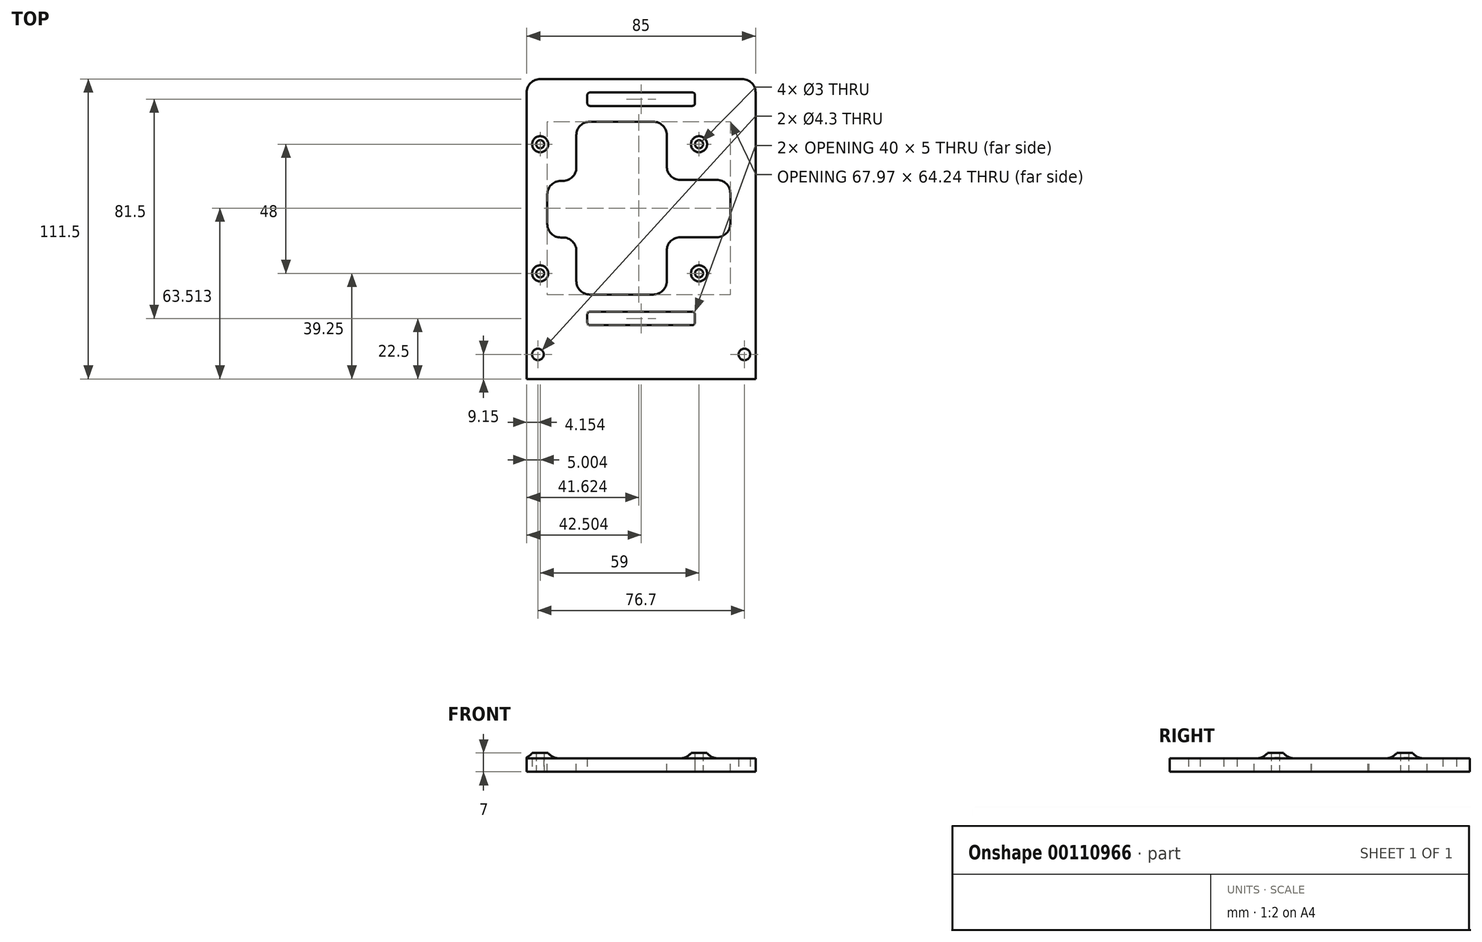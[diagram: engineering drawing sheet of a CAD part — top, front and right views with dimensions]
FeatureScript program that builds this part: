
annotation { "Feature Type Name" : "Feature", "Feature Type Description" : "" }
export const myFeature = defineFeature(function(context is Context, id is Id, definition is map)
    precondition{}
    {
        {
            var Q0;
            Q0=qCreatedBy(makeId("Top.planeOp"),FACE);
            var sketch = newSketch(context, id + "F0", { "sketchPlane" : qUnion([Q0])});
            skLineSegment(sketch, "E0.bottom", {"start": v(-29.26, 0) * mm, "end": v(55.74, 0) * mm});
            skLineSegment(sketch, "E0.top", {"start": v(-29.26, 111.5) * mm, "end": v(55.74, 111.5) * mm});
            skLineSegment(sketch, "E0.left", {"start": v(-29.26, 0) * mm, "end": v(-29.26, 111.5) * mm});
            skLineSegment(sketch, "E0.right", {"start": v(55.74, 0) * mm, "end": v(55.74, 111.5) * mm});
            skLineSegment(sketch, "E1.top", {"start": v(-29.26, 20) * mm, "end": v(55.74, 20) * mm});
            skLineSegment(sketch, "E1.left", {"start": v(-29.26, 0) * mm, "end": v(-29.26, 20) * mm});
            skLineSegment(sketch, "E1.right", {"start": v(55.74, 0) * mm, "end": v(55.74, 20) * mm});
            skLineSegment(sketch, "E2.bottom", {"start": v(-6.76, 20) * mm, "end": v(33.24, 20) * mm});
            skLineSegment(sketch, "E2.top", {"start": v(-6.76, 25) * mm, "end": v(33.24, 25) * mm});
            skLineSegment(sketch, "E2.left", {"start": v(-6.76, 20) * mm, "end": v(-6.76, 25) * mm});
            skLineSegment(sketch, "E2.right", {"start": v(33.24, 20) * mm, "end": v(33.24, 25) * mm});
            skPoint(sketch, "E3", {"position": v(13.24, 111.5) * mm});
            skPoint(sketch, "E4", {"position": v(13.24, 25) * mm});
            skLineSegment(sketch, "E5.top", {"start": v(-29.26, 106.5) * mm, "end": v(55.74, 106.5) * mm});
            skLineSegment(sketch, "E5.left", {"start": v(-29.26, 111.5) * mm, "end": v(-29.26, 106.5) * mm});
            skLineSegment(sketch, "E5.right", {"start": v(55.74, 111.5) * mm, "end": v(55.74, 106.5) * mm});
            skCircle(sketch, "E6", {"center": v(13.24, 63.25) * mm, "radius": 5 * mm});
            skCircle(sketch, "E7", {"center": v(23.24, 53.25) * mm, "radius": 1.5 * mm});
            skCircle(sketch, "E8", {"center": v(3.24, 53.25) * mm, "radius": 1.5 * mm});
            skCircle(sketch, "E9", {"center": v(3.24, 73.25) * mm, "radius": 1.5 * mm});
            skCircle(sketch, "E10", {"center": v(23.24, 73.25) * mm, "radius": 1.5 * mm});
            skLineSegment(sketch, "E11", {"start": v(23.24, 73.25) * mm, "end": v(23.24, 53.25) * mm, "construction": true});
            skLineSegment(sketch, "E12", {"start": v(3.24, 73.25) * mm, "end": v(23.24, 73.25) * mm, "construction": true});
            skPoint(sketch, "E13", {"position": v(23.24, 63.25) * mm});
            skPoint(sketch, "E14", {"position": v(13.24, 73.25) * mm});
            skLineSegment(sketch, "E15", {"start": v(23.24, 73.25) * mm, "end": v(23.24, 106.5) * mm, "construction": true});
            skLineSegment(sketch, "E16", {"start": v(23.24, 53.25) * mm, "end": v(23.24, 20) * mm, "construction": true});
            skCircle(sketch, "E17", {"center": v(-24.26, 87.25) * mm, "radius": 3 * mm});
            skCircle(sketch, "E18", {"center": v(-24.26, 39.25) * mm, "radius": 3 * mm});
            skCircle(sketch, "E19", {"center": v(34.74, 87.25) * mm, "radius": 3 * mm});
            skCircle(sketch, "E20", {"center": v(34.74, 39.25) * mm, "radius": 3 * mm});
            skLineSegment(sketch, "E21", {"start": v(-24.26, 87.25) * mm, "end": v(34.74, 87.25) * mm, "construction": true});
            skLineSegment(sketch, "E22", {"start": v(34.74, 87.25) * mm, "end": v(34.74, 39.25) * mm, "construction": true});
            skCircle(sketch, "E23", {"center": v(-24.26, 87.25) * mm, "radius": 1.5 * mm});
            skCircle(sketch, "E24", {"center": v(-24.26, 39.25) * mm, "radius": 1.5 * mm});
            skCircle(sketch, "E25", {"center": v(34.74, 39.25) * mm, "radius": 1.5 * mm});
            skCircle(sketch, "E26", {"center": v(34.74, 87.25) * mm, "radius": 1.5 * mm});
            skLineSegment(sketch, "E27", {"start": v(34.74, 39.25) * mm, "end": v(34.74, 20) * mm, "construction": true});
            skLineSegment(sketch, "E28", {"start": v(34.74, 87.25) * mm, "end": v(34.74, 106.5) * mm, "construction": true});
            skCircle(sketch, "E29", {"center": v(-25.1, 9.15) * mm, "radius": 2.15 * mm});
            skCircle(sketch, "E30", {"center": v(51.6, 9.15) * mm, "radius": 2.15 * mm});
            skLineSegment(sketch, "E31.bottom", {"start": v(-6.76, 106.5) * mm, "end": v(33.24, 106.5) * mm});
            skLineSegment(sketch, "E31.top", {"start": v(-6.76, 101.5) * mm, "end": v(33.24, 101.5) * mm});
            skLineSegment(sketch, "E31.left", {"start": v(-6.76, 106.5) * mm, "end": v(-6.76, 101.5) * mm});
            skLineSegment(sketch, "E31.right", {"start": v(33.24, 106.5) * mm, "end": v(33.24, 101.5) * mm});
            skSolve(sketch);
        }
        {
            var Q0;
            Q0=qSketchRegion(id+"F0",true);
            var Q1;
            Q1=makeQuery(id+"F0.imprint","IMPRINT",FACE,{"disambiguationData":[TD([[makeQuery(id+"F0.imprint","IMPRINT",EDGE,{"derivedFrom":sQuery(id+"F0.wireOp",EDGE,"E18")}),1.0]])]});
            var Q2;
            Q2=makeQuery(id+"F0.imprint","IMPRINT",FACE,{"disambiguationData":[TD([[makeQuery(id+"F0.imprint","IMPRINT",EDGE,{"derivedFrom":sQuery(id+"F0.wireOp",EDGE,"E17")}),1.0]])]});
            var Q3;
            Q3=makeQuery(id+"F0.imprint","IMPRINT",FACE,{"disambiguationData":[TD([[makeQuery(id+"F0.imprint","IMPRINT",EDGE,{"derivedFrom":sQuery(id+"F0.wireOp",EDGE,"E20")}),1.0]])]});
            var Q4;
            Q4=makeQuery(id+"F0.imprint","IMPRINT",FACE,{"disambiguationData":[TD([[makeQuery(id+"F0.imprint","IMPRINT",EDGE,{"derivedFrom":sQuery(id+"F0.wireOp",EDGE,"E19")}),1.0]])]});
            var Q5;
            Q5=makeQuery(id+"F0.imprint","IMPRINT",FACE,{"disambiguationData":[TD([[makeQuery(id+"F0.imprint","IMPRINT",EDGE,{"derivedFrom":sQuery(id+"F0.wireOp",EDGE,"E6")}),1.0]])]});
            var Q6;
            Q6=makeQuery(id+"F0.imprint","IMPRINT",FACE,{"disambiguationData":[TD([[makeQuery(id+"F0.imprint","IMPRINT",EDGE,{"derivedFrom":sQuery(id+"F0.wireOp",EDGE,"E9")}),1.0]])]});
            var Q7;
            Q7=makeQuery(id+"F0.imprint","IMPRINT",FACE,{"disambiguationData":[TD([[makeQuery(id+"F0.imprint","IMPRINT",EDGE,{"derivedFrom":sQuery(id+"F0.wireOp",EDGE,"E8")}),1.0]])]});
            var Q8;
            Q8=makeQuery(id+"F0.imprint","IMPRINT",FACE,{"disambiguationData":[TD([[makeQuery(id+"F0.imprint","IMPRINT",EDGE,{"derivedFrom":sQuery(id+"F0.wireOp",EDGE,"E7")}),1.0]])]});
            var Q9;
            Q9=makeQuery(id+"F0.imprint","IMPRINT",FACE,{"disambiguationData":[TD([[makeQuery(id+"F0.imprint","IMPRINT",EDGE,{"derivedFrom":sQuery(id+"F0.wireOp",EDGE,"E10")}),1.0]])]});
            extrude(context, id + "F1", {"entities" : qUnion([Q0, Q1, Q2, Q3, Q4, Q5, Q6, Q7, Q8, Q9]), "depth" : 5 * mm});
        }
        {
            var Q0;
            Q0=makeQuery(id+"F1.opExtrude","SWEPT_EDGE",EDGE,{"disambiguationData":[OSD([sQuery(id+"F0.wireOp",EDGE,"E2.top"),sQuery(id+"F0.wireOp",EDGE,"E2.left")])]});
            var Q1;
            Q1=makeQuery(id+"F1.opExtrude","SWEPT_EDGE",EDGE,{"disambiguationData":[OSD([sQuery(id+"F0.wireOp",EDGE,"E2.top"),sQuery(id+"F0.wireOp",EDGE,"E2.right")])]});
            var Q2;
            Q2=makeQuery(id+"F1.opExtrude","SWEPT_EDGE",EDGE,{"disambiguationData":[OSD([sQuery(id+"F0.wireOp",EDGE,"E1.top"),sQuery(id+"F0.wireOp",EDGE,"E2.bottom"),sQuery(id+"F0.wireOp",EDGE,"E2.left")])]});
            var Q3;
            Q3=makeQuery(id+"F1.opExtrude","SWEPT_EDGE",EDGE,{"disambiguationData":[OSD([sQuery(id+"F0.wireOp",EDGE,"E1.top"),sQuery(id+"F0.wireOp",EDGE,"E2.bottom"),sQuery(id+"F0.wireOp",EDGE,"E2.right")])]});
            var Q4;
            Q4=makeQuery(id+"F1.opExtrude","SWEPT_EDGE",EDGE,{"disambiguationData":[OSD([sQuery(id+"F0.wireOp",EDGE,"E31.top"),sQuery(id+"F0.wireOp",EDGE,"E31.left")])]});
            var Q5;
            Q5=makeQuery(id+"F1.opExtrude","SWEPT_EDGE",EDGE,{"disambiguationData":[OSD([sQuery(id+"F0.wireOp",EDGE,"E5.top"),sQuery(id+"F0.wireOp",EDGE,"E31.bottom"),sQuery(id+"F0.wireOp",EDGE,"E31.left")])]});
            var Q6;
            Q6=makeQuery(id+"F1.opExtrude","SWEPT_EDGE",EDGE,{"disambiguationData":[OSD([sQuery(id+"F0.wireOp",EDGE,"E5.top"),sQuery(id+"F0.wireOp",EDGE,"E31.bottom"),sQuery(id+"F0.wireOp",EDGE,"E31.right")])]});
            var Q7;
            Q7=makeQuery(id+"F1.opExtrude","SWEPT_EDGE",EDGE,{"disambiguationData":[OSD([sQuery(id+"F0.wireOp",EDGE,"E31.top"),sQuery(id+"F0.wireOp",EDGE,"E31.right")])]});
            fillet(context, id + "F2", {"entities" : qUnion([Q0, Q1, Q2, Q3, Q4, Q5, Q6, Q7]), "radius" : 1 * mm, "tangentPropagation" : true, "allowEdgeOverflow" : false});
        }
        {
            var Q0;
            {var subQ0=sQuery(id+"F0.wireOp",EDGE,"E5.left");var subQ1=sQuery(id+"F0.wireOp",EDGE,"E0.top");Q0=makeQuery(id+"FNY0aRx3992dt0J_1.boolean.opBoolean","MERGE",EDGE,{"derivedFrom":[makeQuery(id+"F1.opExtrude","SWEPT_EDGE",EDGE,{"disambiguationData":[OSD([subQ1,subQ0])]}),makeQuery(id+"FNY0aRx3992dt0J_1.opExtrude","SWEPT_EDGE",EDGE,{"disambiguationData":[OSD([subQ1,subQ0])]})]});}
            var Q1;
            {var subQ0=sQuery(id+"F0.wireOp",EDGE,"E1.left");var subQ1=sQuery(id+"F0.wireOp",EDGE,"E0.bottom");Q1=makeQuery(id+"FNY0aRx3992dt0J_1.boolean.opBoolean","MERGE",EDGE,{"derivedFrom":[makeQuery(id+"F1.opExtrude","SWEPT_EDGE",EDGE,{"disambiguationData":[OSD([subQ1,subQ0])]}),makeQuery(id+"FNY0aRx3992dt0J_1.opExtrude","SWEPT_EDGE",EDGE,{"disambiguationData":[OSD([subQ1,subQ0])]})]});}
            var Q2;
            Q2=makeQuery(id+"F1.opExtrude","SWEPT_EDGE",EDGE,{"disambiguationData":[OSD([sQuery(id+"F0.wireOp",EDGE,"E0.bottom"),sQuery(id+"F0.wireOp",EDGE,"E1.left")])]});
            var Q3;
            Q3=makeQuery(id+"F1.opExtrude","SWEPT_EDGE",EDGE,{"disambiguationData":[OSD([sQuery(id+"F0.wireOp",EDGE,"E0.bottom"),sQuery(id+"F0.wireOp",EDGE,"E1.right")])]});
            var Q4;
            Q4=makeQuery(id+"F1.opExtrude","SWEPT_EDGE",EDGE,{"disambiguationData":[OSD([sQuery(id+"F0.wireOp",EDGE,"E0.top"),sQuery(id+"F0.wireOp",EDGE,"E5.right")])]});
            fillet(context, id + "F3", {"entities" : qUnion([Q0, Q1, Q2, Q3, Q4]), "radius" : 5 * mm, "tangentPropagation" : true, "allowEdgeOverflow" : false});
        }
        {
            var Q0;
            Q0=makeQuery(id+"F0.imprint","IMPRINT",FACE,{"disambiguationData":[TD([[makeQuery(id+"F0.imprint","IMPRINT",EDGE,{"derivedFrom":sQuery(id+"F0.wireOp",EDGE,"E17")}),1.0]])]});
            var Q1;
            Q1=makeQuery(id+"F0.imprint","IMPRINT",FACE,{"disambiguationData":[TD([[makeQuery(id+"F0.imprint","IMPRINT",EDGE,{"derivedFrom":sQuery(id+"F0.wireOp",EDGE,"E18")}),1.0]])]});
            var Q2;
            Q2=makeQuery(id+"F0.imprint","IMPRINT",FACE,{"disambiguationData":[TD([[makeQuery(id+"F0.imprint","IMPRINT",EDGE,{"derivedFrom":sQuery(id+"F0.wireOp",EDGE,"E19")}),1.0]])]});
            var Q3;
            Q3=makeQuery(id+"F0.imprint","IMPRINT",FACE,{"disambiguationData":[TD([[makeQuery(id+"F0.imprint","IMPRINT",EDGE,{"derivedFrom":sQuery(id+"F0.wireOp",EDGE,"E20")}),1.0]])]});
            extrude(context, id + "F4", {"entities" : qUnion([Q0, Q1, Q2, Q3]), "operationType" : NewBodyOperationType.ADD, "depth" : 7 * mm});
        }
        {
            var Q0;
            Q0=makeQuery(id+"F4.boolean.opBoolean","INTERSECT",EDGE,{"derivedFrom":[makeQuery(id+"F1.opExtrude","CAP_FACE",FACE,{"disambiguationData":[OSD([sQuery(id+"F0.wireOp",EDGE,"E0.left"),sQuery(id+"F0.wireOp",EDGE,"E0.right"),sQuery(id+"F0.wireOp",EDGE,"E0.bottom"),sQuery(id+"F0.wireOp",EDGE,"E1.left"),sQuery(id+"F0.wireOp",EDGE,"E1.right"),sQuery(id+"F0.wireOp",EDGE,"E2.bottom"),sQuery(id+"F0.wireOp",EDGE,"E2.top"),sQuery(id+"F0.wireOp",EDGE,"E2.left"),sQuery(id+"F0.wireOp",EDGE,"E2.right"),sQuery(id+"F0.wireOp",EDGE,"E0.top"),sQuery(id+"F0.wireOp",EDGE,"E5.left"),sQuery(id+"F0.wireOp",EDGE,"E5.right"),sQuery(id+"F0.wireOp",EDGE,"E6"),sQuery(id+"F0.wireOp",EDGE,"E7"),sQuery(id+"F0.wireOp",EDGE,"E8"),sQuery(id+"F0.wireOp",EDGE,"E9"),sQuery(id+"F0.wireOp",EDGE,"E10")])],"isStart":false}),makeQuery(id+"F4.opExtrude","SWEPT_FACE",FACE,{"disambiguationData":[OSD([sQuery(id+"F0.wireOp",EDGE,"E17")])]})]});
            var Q1;
            Q1=makeQuery(id+"F4.boolean.opBoolean","INTERSECT",EDGE,{"derivedFrom":[makeQuery(id+"F1.opExtrude","CAP_FACE",FACE,{"disambiguationData":[OSD([sQuery(id+"F0.wireOp",EDGE,"E0.left"),sQuery(id+"F0.wireOp",EDGE,"E0.right"),sQuery(id+"F0.wireOp",EDGE,"E0.bottom"),sQuery(id+"F0.wireOp",EDGE,"E1.left"),sQuery(id+"F0.wireOp",EDGE,"E1.right"),sQuery(id+"F0.wireOp",EDGE,"E2.bottom"),sQuery(id+"F0.wireOp",EDGE,"E2.top"),sQuery(id+"F0.wireOp",EDGE,"E2.left"),sQuery(id+"F0.wireOp",EDGE,"E2.right"),sQuery(id+"F0.wireOp",EDGE,"E0.top"),sQuery(id+"F0.wireOp",EDGE,"E5.left"),sQuery(id+"F0.wireOp",EDGE,"E5.right"),sQuery(id+"F0.wireOp",EDGE,"E6"),sQuery(id+"F0.wireOp",EDGE,"E7"),sQuery(id+"F0.wireOp",EDGE,"E8"),sQuery(id+"F0.wireOp",EDGE,"E9"),sQuery(id+"F0.wireOp",EDGE,"E10")])],"isStart":false}),makeQuery(id+"F4.opExtrude","SWEPT_FACE",FACE,{"disambiguationData":[OSD([sQuery(id+"F0.wireOp",EDGE,"E18")])]})]});
            var Q2;
            Q2=makeQuery(id+"F4.boolean.opBoolean","INTERSECT",EDGE,{"derivedFrom":[makeQuery(id+"F1.opExtrude","CAP_FACE",FACE,{"disambiguationData":[OSD([sQuery(id+"F0.wireOp",EDGE,"E0.left"),sQuery(id+"F0.wireOp",EDGE,"E0.right"),sQuery(id+"F0.wireOp",EDGE,"E0.bottom"),sQuery(id+"F0.wireOp",EDGE,"E1.left"),sQuery(id+"F0.wireOp",EDGE,"E1.right"),sQuery(id+"F0.wireOp",EDGE,"E2.bottom"),sQuery(id+"F0.wireOp",EDGE,"E2.top"),sQuery(id+"F0.wireOp",EDGE,"E2.left"),sQuery(id+"F0.wireOp",EDGE,"E2.right"),sQuery(id+"F0.wireOp",EDGE,"E0.top"),sQuery(id+"F0.wireOp",EDGE,"E5.left"),sQuery(id+"F0.wireOp",EDGE,"E5.right"),sQuery(id+"F0.wireOp",EDGE,"E6"),sQuery(id+"F0.wireOp",EDGE,"E7"),sQuery(id+"F0.wireOp",EDGE,"E8"),sQuery(id+"F0.wireOp",EDGE,"E9"),sQuery(id+"F0.wireOp",EDGE,"E10")])],"isStart":false}),makeQuery(id+"F4.opExtrude","SWEPT_FACE",FACE,{"disambiguationData":[OSD([sQuery(id+"F0.wireOp",EDGE,"E20")])]})]});
            var Q3;
            Q3=makeQuery(id+"F4.boolean.opBoolean","INTERSECT",EDGE,{"derivedFrom":[makeQuery(id+"F1.opExtrude","CAP_FACE",FACE,{"disambiguationData":[OSD([sQuery(id+"F0.wireOp",EDGE,"E0.left"),sQuery(id+"F0.wireOp",EDGE,"E0.right"),sQuery(id+"F0.wireOp",EDGE,"E0.bottom"),sQuery(id+"F0.wireOp",EDGE,"E1.left"),sQuery(id+"F0.wireOp",EDGE,"E1.right"),sQuery(id+"F0.wireOp",EDGE,"E2.bottom"),sQuery(id+"F0.wireOp",EDGE,"E2.top"),sQuery(id+"F0.wireOp",EDGE,"E2.left"),sQuery(id+"F0.wireOp",EDGE,"E2.right"),sQuery(id+"F0.wireOp",EDGE,"E0.top"),sQuery(id+"F0.wireOp",EDGE,"E5.left"),sQuery(id+"F0.wireOp",EDGE,"E5.right"),sQuery(id+"F0.wireOp",EDGE,"E6"),sQuery(id+"F0.wireOp",EDGE,"E7"),sQuery(id+"F0.wireOp",EDGE,"E8"),sQuery(id+"F0.wireOp",EDGE,"E9"),sQuery(id+"F0.wireOp",EDGE,"E10")])],"isStart":false}),makeQuery(id+"F4.opExtrude","SWEPT_FACE",FACE,{"disambiguationData":[OSD([sQuery(id+"F0.wireOp",EDGE,"E19")])]})]});
            fillet(context, id + "F5", {"entities" : qUnion([Q0, Q1, Q2, Q3]), "radius" : 5 * mm, "tangentPropagation" : true, "allowEdgeOverflow" : false});
        }
        {
            var Q0;
            Q0=makeQuery(id+"F1.opExtrude","CAP_FACE",FACE,{"disambiguationData":[OSD([sQuery(id+"F0.wireOp",EDGE,"E0.left"),sQuery(id+"F0.wireOp",EDGE,"E0.right"),sQuery(id+"F0.wireOp",EDGE,"E0.bottom"),sQuery(id+"F0.wireOp",EDGE,"E1.left"),sQuery(id+"F0.wireOp",EDGE,"E1.right"),sQuery(id+"F0.wireOp",EDGE,"E2.bottom"),sQuery(id+"F0.wireOp",EDGE,"E2.top"),sQuery(id+"F0.wireOp",EDGE,"E2.left"),sQuery(id+"F0.wireOp",EDGE,"E2.right"),sQuery(id+"F0.wireOp",EDGE,"E0.top"),sQuery(id+"F0.wireOp",EDGE,"E5.left"),sQuery(id+"F0.wireOp",EDGE,"E5.right"),sQuery(id+"F0.wireOp",EDGE,"E23"),sQuery(id+"F0.wireOp",EDGE,"E24"),sQuery(id+"F0.wireOp",EDGE,"E25"),sQuery(id+"F0.wireOp",EDGE,"E26"),sQuery(id+"F0.wireOp",EDGE,"E29"),sQuery(id+"F0.wireOp",EDGE,"E30")])],"isStart":false});
            var sketch = newSketch(context, id + "F6", { "sketchPlane" : qUnion([Q0])});
            skLineSegment(sketch, "E32.bottom", {"start": v(-10.84, 95.63) * mm, "end": v(22.74, 95.63) * mm});
            skLineSegment(sketch, "E32.top", {"start": v(-10.84, 31.4) * mm, "end": v(22.74, 31.4) * mm});
            skLineSegment(sketch, "E32.left", {"start": v(-10.84, 95.63) * mm, "end": v(-10.84, 31.4) * mm});
            skLineSegment(sketch, "E32.right", {"start": v(22.74, 95.63) * mm, "end": v(22.74, 31.4) * mm});
            skLineSegment(sketch, "E33.bottom", {"start": v(-21.62, 73.63) * mm, "end": v(-10.84, 73.63) * mm});
            skLineSegment(sketch, "E33.top", {"start": v(-21.62, 52.6) * mm, "end": v(-10.84, 52.6) * mm});
            skLineSegment(sketch, "E33.left", {"start": v(-21.62, 73.63) * mm, "end": v(-21.62, 52.6) * mm});
            skLineSegment(sketch, "E33.right", {"start": v(-10.84, 73.63) * mm, "end": v(-10.84, 52.6) * mm});
            skLineSegment(sketch, "E34.bottom", {"start": v(22.74, 74.04) * mm, "end": v(46.35, 74.04) * mm});
            skLineSegment(sketch, "E34.top", {"start": v(22.74, 52.69) * mm, "end": v(46.35, 52.69) * mm});
            skLineSegment(sketch, "E34.left", {"start": v(22.74, 74.04) * mm, "end": v(22.74, 52.69) * mm});
            skLineSegment(sketch, "E34.right", {"start": v(46.35, 74.04) * mm, "end": v(46.35, 52.69) * mm});
            skSolve(sketch);
        }
        {
            var Q0;
            Q0=qSketchRegion(id+"F6",true);
            extrude(context, id + "F7", {"entities" : qUnion([Q0]), "operationType" : NewBodyOperationType.REMOVE, "oppositeDirection" : true, "depth" : 25 * mm});
        }
        {
            var Q0;
            Q0=makeQuery(id+"F7.boolean.opBoolean","COPY",EDGE,{"derivedFrom":makeQuery(id+"F7.opExtrude","SWEPT_EDGE",EDGE,{"disambiguationData":[OSD([sQuery(id+"F6.wireOp",EDGE,"E32.left"),sQuery(id+"F6.wireOp",EDGE,"E33.bottom"),sQuery(id+"F6.wireOp",EDGE,"E33.right")])]})});
            var Q1;
            Q1=makeQuery(id+"F7.boolean.opBoolean","COPY",EDGE,{"derivedFrom":makeQuery(id+"F7.opExtrude","SWEPT_EDGE",EDGE,{"disambiguationData":[OSD([sQuery(id+"F6.wireOp",EDGE,"E32.right"),sQuery(id+"F6.wireOp",EDGE,"E34.bottom"),sQuery(id+"F6.wireOp",EDGE,"E34.left")])]})});
            var Q2;
            Q2=makeQuery(id+"F7.boolean.opBoolean","COPY",EDGE,{"derivedFrom":makeQuery(id+"F7.opExtrude","SWEPT_EDGE",EDGE,{"disambiguationData":[OSD([sQuery(id+"F6.wireOp",EDGE,"E32.right"),sQuery(id+"F6.wireOp",EDGE,"E34.top"),sQuery(id+"F6.wireOp",EDGE,"E34.left")])]})});
            var Q3;
            Q3=makeQuery(id+"F7.boolean.opBoolean","COPY",EDGE,{"derivedFrom":makeQuery(id+"F7.opExtrude","SWEPT_EDGE",EDGE,{"disambiguationData":[OSD([sQuery(id+"F6.wireOp",EDGE,"E32.left"),sQuery(id+"F6.wireOp",EDGE,"E33.top"),sQuery(id+"F6.wireOp",EDGE,"E33.right")])]})});
            var Q4;
            Q4=makeQuery(id+"F7.boolean.opBoolean","COPY",EDGE,{"derivedFrom":makeQuery(id+"F7.opExtrude","SWEPT_EDGE",EDGE,{"disambiguationData":[OSD([sQuery(id+"F6.wireOp",EDGE,"E33.top"),sQuery(id+"F6.wireOp",EDGE,"E33.left")])]})});
            var Q5;
            Q5=makeQuery(id+"F7.boolean.opBoolean","COPY",EDGE,{"derivedFrom":makeQuery(id+"F7.opExtrude","SWEPT_EDGE",EDGE,{"disambiguationData":[OSD([sQuery(id+"F6.wireOp",EDGE,"E33.bottom"),sQuery(id+"F6.wireOp",EDGE,"E33.left")])]})});
            var Q6;
            Q6=makeQuery(id+"F7.boolean.opBoolean","COPY",EDGE,{"derivedFrom":makeQuery(id+"F7.opExtrude","SWEPT_EDGE",EDGE,{"disambiguationData":[OSD([sQuery(id+"F6.wireOp",EDGE,"E32.bottom"),sQuery(id+"F6.wireOp",EDGE,"E32.left")])]})});
            var Q7;
            Q7=makeQuery(id+"F7.boolean.opBoolean","COPY",EDGE,{"derivedFrom":makeQuery(id+"F7.opExtrude","SWEPT_EDGE",EDGE,{"disambiguationData":[OSD([sQuery(id+"F6.wireOp",EDGE,"E32.bottom"),sQuery(id+"F6.wireOp",EDGE,"E32.right")])]})});
            var Q8;
            Q8=makeQuery(id+"F7.boolean.opBoolean","COPY",EDGE,{"derivedFrom":makeQuery(id+"F7.opExtrude","SWEPT_EDGE",EDGE,{"disambiguationData":[OSD([sQuery(id+"F6.wireOp",EDGE,"E34.bottom"),sQuery(id+"F6.wireOp",EDGE,"E34.right")])]})});
            var Q9;
            Q9=makeQuery(id+"F7.boolean.opBoolean","COPY",EDGE,{"derivedFrom":makeQuery(id+"F7.opExtrude","SWEPT_EDGE",EDGE,{"disambiguationData":[OSD([sQuery(id+"F6.wireOp",EDGE,"E34.top"),sQuery(id+"F6.wireOp",EDGE,"E34.right")])]})});
            var Q10;
            Q10=makeQuery(id+"F7.boolean.opBoolean","COPY",EDGE,{"derivedFrom":makeQuery(id+"F7.opExtrude","SWEPT_EDGE",EDGE,{"disambiguationData":[OSD([sQuery(id+"F6.wireOp",EDGE,"E32.top"),sQuery(id+"F6.wireOp",EDGE,"E32.right")])]})});
            var Q11;
            Q11=makeQuery(id+"F7.boolean.opBoolean","COPY",EDGE,{"derivedFrom":makeQuery(id+"F7.opExtrude","SWEPT_EDGE",EDGE,{"disambiguationData":[OSD([sQuery(id+"F6.wireOp",EDGE,"E32.top"),sQuery(id+"F6.wireOp",EDGE,"E32.left")])]})});
            fillet(context, id + "F8", {"entities" : qUnion([Q0, Q1, Q2, Q3, Q4, Q5, Q6, Q7, Q8, Q9, Q10, Q11]), "radius" : 5 * mm, "tangentPropagation" : true, "allowEdgeOverflow" : false});
        }
    });
